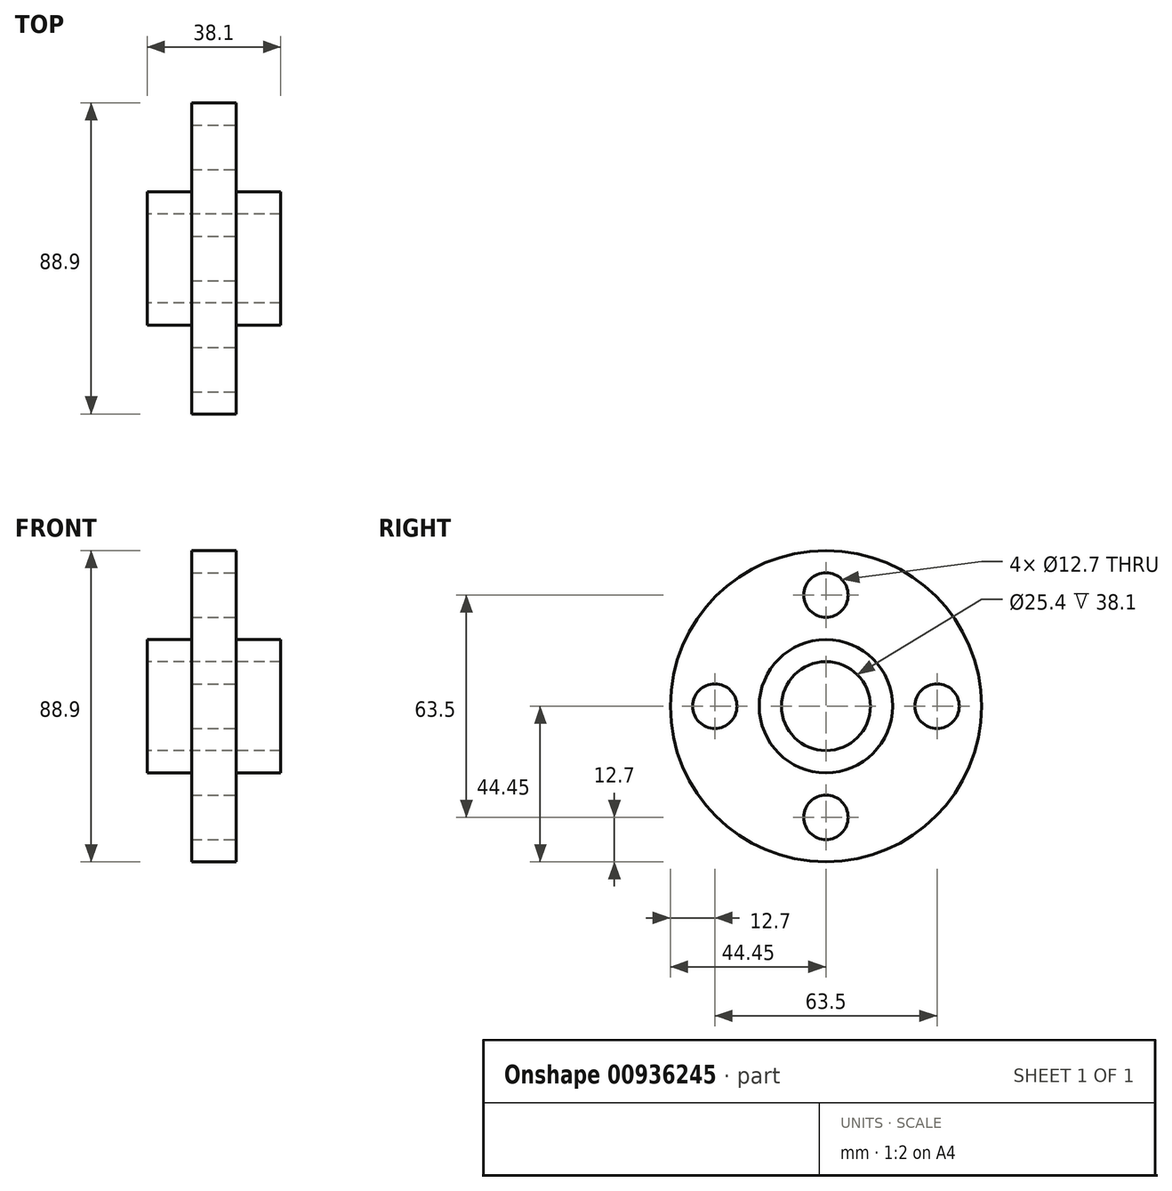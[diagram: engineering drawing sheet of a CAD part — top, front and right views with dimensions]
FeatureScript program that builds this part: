
annotation { "Feature Type Name" : "Feature", "Feature Type Description" : "" }
export const myFeature = defineFeature(function(context is Context, id is Id, definition is map)
    precondition{}
    {
        {
            var Q0;
            Q0=qCreatedBy(makeId("Front.planeOp"),FACE);
            var sketch = newSketch(context, id + "F0", { "sketchPlane" : qUnion([Q0])});
            skLineSegment(sketch, "E0", {"start": v(-19.05, 19.05) * mm, "end": v(-6.35, 19.05) * mm});
            skLineSegment(sketch, "E1", {"start": v(-6.35, 19.05) * mm, "end": v(-6.35, 44.45) * mm});
            skLineSegment(sketch, "E2", {"start": v(-6.35, 44.45) * mm, "end": v(6.35, 44.45) * mm});
            skLineSegment(sketch, "E3", {"start": v(6.35, 44.45) * mm, "end": v(6.35, 19.05) * mm});
            skLineSegment(sketch, "E4", {"start": v(6.35, 19.05) * mm, "end": v(19.05, 19.05) * mm});
            skLineSegment(sketch, "E5", {"start": v(-19.05, 19.05) * mm, "end": v(-19.05, 12.7) * mm});
            skLineSegment(sketch, "E6", {"start": v(19.05, 19.05) * mm, "end": v(19.05, 12.7) * mm});
            skLineSegment(sketch, "E7", {"start": v(-19.05, 12.7) * mm, "end": v(-19.05, 0) * mm, "construction": true});
            skLineSegment(sketch, "E8", {"start": v(-19.05, 12.7) * mm, "end": v(19.05, 12.7) * mm});
            skLineSegment(sketch, "E9", {"start": v(-19.05, 0) * mm, "end": v(18.98, 0) * mm, "construction": true});
            skSolve(sketch);
        }
        {
            var Q0;
            Q0=makeQuery(id+"F0.imprint","IMPRINT",FACE,{"disambiguationData":[TD([[makeQuery(id+"F0.imprint","IMPRINT",EDGE,{"derivedFrom":sQuery(id+"F0.wireOp",EDGE,"E0")}),-1.0]])]});
            var Q1;
            Q1=sQuery(id+"F0.wireOp",EDGE,"E9");
            revolve(context, id + "F1", {"entities" : qUnion([Q0]), "axis" : qUnion([Q1]), "revolveType" : RevolveType.FULL});
        }
        {
            var Q0;
            Q0=makeQuery(id+"F1.opRevolve","SWEPT_FACE",FACE,{"disambiguationData":[OSD([sQuery(id+"F0.wireOp",EDGE,"E3")])]});
            var sketch = newSketch(context, id + "F2", { "sketchPlane" : qUnion([Q0])});
            skCircle(sketch, "E10", {"center": v(0, 0) * mm, "radius": 31.75 * mm, "construction": true});
            skCircle(sketch, "E11", {"center": v(-31.75, 0) * mm, "radius": 6.35 * mm});
            skCircle(sketch, "E12.1.0", {"center": v(0, -31.75) * mm, "radius": 6.35 * mm});
            skCircle(sketch, "E12.2.0", {"center": v(31.75, 0) * mm, "radius": 6.35 * mm});
            skCircle(sketch, "E12.3.0", {"center": v(0, 31.75) * mm, "radius": 6.35 * mm});
            skSolve(sketch);
        }
        {
            var Q0;
            Q0=makeQuery(id+"F2.imprint","IMPRINT",FACE,{"disambiguationData":[TD([[makeQuery(id+"F2.imprint","IMPRINT",EDGE,{"derivedFrom":sQuery(id+"F2.wireOp",EDGE,"E12.1.0")}),1.0]])]});
            var Q1;
            Q1=makeQuery(id+"F2.imprint","IMPRINT",FACE,{"disambiguationData":[TD([[makeQuery(id+"F2.imprint","IMPRINT",EDGE,{"derivedFrom":sQuery(id+"F2.wireOp",EDGE,"E12.2.0")}),1.0]])]});
            var Q2;
            Q2=makeQuery(id+"F2.imprint","IMPRINT",FACE,{"disambiguationData":[TD([[makeQuery(id+"F2.imprint","IMPRINT",EDGE,{"derivedFrom":sQuery(id+"F2.wireOp",EDGE,"E12.3.0")}),1.0]])]});
            var Q3;
            Q3=makeQuery(id+"F2.imprint","IMPRINT",FACE,{"disambiguationData":[TD([[makeQuery(id+"F2.imprint","IMPRINT",EDGE,{"derivedFrom":sQuery(id+"F2.wireOp",EDGE,"E11")}),1.0]])]});
            extrude(context, id + "F3", {"entities" : qUnion([Q0, Q1, Q2, Q3]), "operationType" : NewBodyOperationType.REMOVE, "endBound" : BoundingType.THROUGH_ALL, "oppositeDirection" : true, "depth" : 25.4 * mm});
        }
    });
